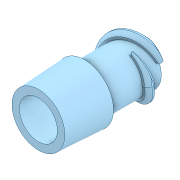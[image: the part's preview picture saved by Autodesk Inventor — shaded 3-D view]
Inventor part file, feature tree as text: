
AUTODESK INVENTOR PART (.ipt)
format: ipt  version: 2022 (Build 260153000, 153)  size: 1,602,048 bytes
history: native  units: mm
features: extrude x2, sketch x2, imported_body x1
ambient origin geometry x8: Origin, YZ Plane, XZ Plane, XY Plane, X Axis, Y Axis, Z Axis, Center Point
bodies: Volumenkörper1 (feature_tree)
feature tree (5):
  extrude  "Extrusion1"  Depth=10.0mm
  extrude  "Extrusion2"  [1 undecoded]
  sketch  "Skizze1"  dims[d0=10.0mm d1=0.0mm d2=7.5mm]
  sketch  "Skizze2"  dims[d3=6.0mm d4=-0.523599mm]
  imported_body  "Basis1"
note: 1 required parameter value undecoded (feature->parameter linkage not recoverable at this tier; creation-order binding heuristic only, values carry confidence <= 0.55)
